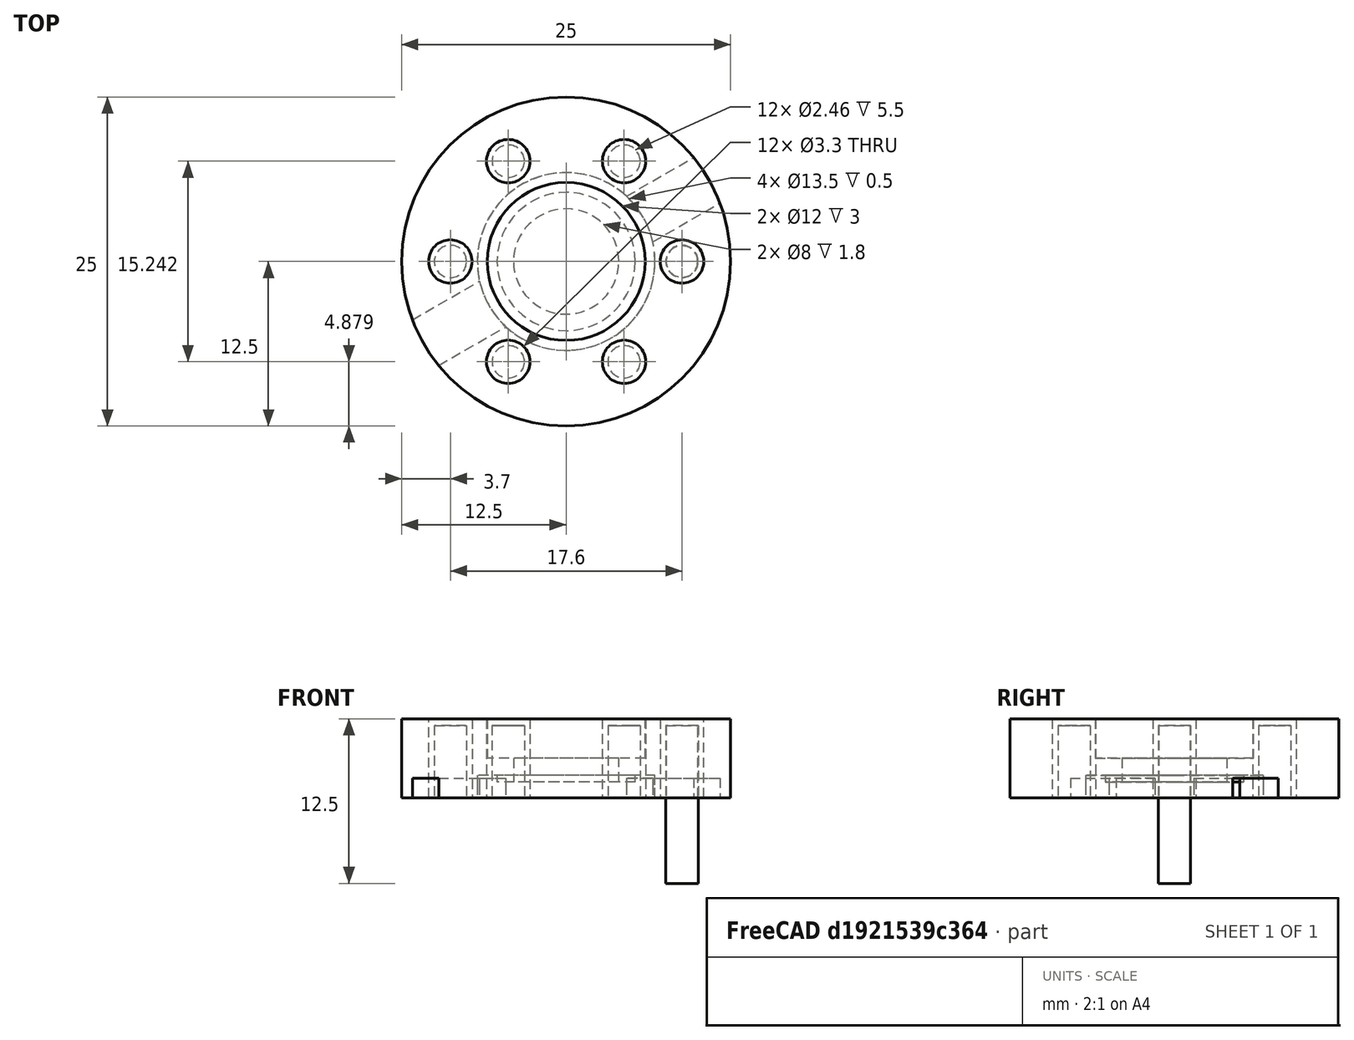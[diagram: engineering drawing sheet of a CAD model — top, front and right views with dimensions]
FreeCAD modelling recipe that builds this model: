
FCSTD DOCUMENT  (FreeCAD 1.0R1.0rc2)
Label: CFFlange_NoKnife
License: All rights reserved
LicenseURL: http://en.wikipedia.org/wiki/All_rights_reserved
objects: Part::Cylinder×32, Part::Cut×32, Part::MultiFuse×10, Part::Box×8, Part::FeaturePython×8, Part::Cone×4, Spreadsheet::Sheet×1
note: 88 computed .brp shape members not serialized (recipe doc carries the construction recipe); baked Part::Feature solids carry a one-line shape summary decoded from their .brp

FEATURE [Part::Box] Box  label="Cube"
  AttacherType = Attacher::AttachEngine3D
  Height = 1.5
  Length = 6.75
  Placement = pos=(6.25,-2,0) rot=(0,0,1;0rad)
  Width = 4
  expr: .Placement.Base.x = <<ConflatFlange001>>.cf_sealrecess / 2 - 0.5
  expr: .Placement.Base.y = -2
  expr: Length = (<<ConflatFlange001>>.cf_od - <<ConflatFlange001>>.cf_sealrecess) / 2 + 1
FEATURE [Part::Box] Box001  label="Cube001"
  AttacherType = Attacher::AttachEngine3D
  Height = 1.5
  Length = 6.75
  Placement = pos=(-13,-2,0) rot=(0,0,1;0rad)
  Width = 4
  expr: .Placement.Base.x = -<<ConflatFlange001>>.cf_sealrecess / 2 + 0.5 - ((<<ConflatFlange001>>.cf_od - <<ConflatFlange001>>.cf_sealrecess) / 2 + 1)
  expr: .Placement.Base.y = -2
  expr: Length = (<<ConflatFlange001>>.cf_od - <<ConflatFlange001>>.cf_sealrecess) / 2 + 1
FEATURE [Part::Cone] Cone
  Angle = 360
  AttacherType = Attacher::AttachEngine3D
  Height = 0.22
  Radius1 = 5.25
  Radius2 = 6.75
  expr: Height = 1.2 - 0.98
  expr: Radius1 = <<ConflatFlange001>>.cf_knife / 2
  expr: Radius2 = <<ConflatFlange001>>.cf_sealrecess / 2
FEATURE [Part::Cylinder] Cylinder  label="Blank"
  Angle = 360
  AttacherType = Attacher::AttachEngine3D
  FirstAngle = 0
  Height = 6
  Radius = 12.5
  SecondAngle = 0
  expr: Height = <<ConflatFlange001>>.cf_thickness
  expr: Radius = <<ConflatFlange001>>.cf_od / 2
FEATURE [Part::Cylinder] Cylinder001  label="SealRecess"
  Angle = 360
  AttacherType = Attacher::AttachEngine3D
  FirstAngle = 0
  Height = 1.2
  Radius = 6.75
  SecondAngle = 0
  expr: Radius = <<ConflatFlange001>>.cf_sealrecess / 2
FEATURE [Part::Cut] Cut
  Base = -> Cylinder
  Tool = -> Cylinder001
FEATURE [Part::Cylinder] Cylinder002  label="Cylinder"
  Angle = 360
  AttacherType = Attacher::AttachEngine3D
  FirstAngle = 0
  Height = 0.22
  Radius = 5.25
  SecondAngle = 0
  expr: Height = 1.2 - 0.98
  expr: Radius = <<ConflatFlange001>>.cf_knife / 2
FEATURE [Part::Cut] Cut001  label="KnifeEdge"
  Base = -> Cone
  Placement = pos=(0,0,0.98) rot=(0,0,1;0rad)
  Tool = -> Cylinder002
FEATURE [Part::Cylinder] Cylinder003
  Angle = 360
  AttacherType = Attacher::AttachEngine3D
  FirstAngle = 0
  Height = 6
  Placement = pos=(8.8,0,0) rot=(0,0,1;0rad)
  Radius = 1.65
  SecondAngle = 0
  expr: .Placement.Base.x = <<ConflatFlange001>>.cf_boltcircle / 2
  expr: Height = <<ConflatFlange001>>.cf_thickness
  expr: Radius = <<ConflatFlange001>>.cf_boltdia / 2
FEATURE [Part::FeaturePython] Array  label="BoltHoleArray"  # Draft array (typed FeaturePython)
  AlwaysSyncPlacement = false
  Angle = 360
  ArrayType = 1
  Axis = (0,0,1)
  Base = -> Cylinder003
  Center = (0,0,0)
  Count = 6
  ExpandArray = false
  Fuse = false
  IntervalAxis = (0,0,0)
  IntervalX = (50,0,0)
  IntervalY = (0,50,0)
  IntervalZ = (0,0,50)
  NumberCircles = 3
  NumberPolar = 6
  NumberX = 2
  NumberY = 2
  NumberZ = 1
  PlacementList = 6 placements: [(8.8,0,0),(4.4,7.62102,0),(-4.4,7.62102,0),(-8.8,1.07769e-15,0),(-4.4,-7.62102,0),(4.4,-7.62102,0)]
  RadialDistance = 50
  ScaleList = (6) [(1,1,1),(1,1,1),(1,1,1),(1,1,1),(1,1,1),(1,1,1)]
  Symmetry = 1
  TangentialDistance = 25
  expr: NumberPolar = <<ConflatFlange001>>.cf_nbolts
FEATURE [Part::Cylinder] Cylinder024
  Angle = 360
  AttacherType = Attacher::AttachEngine3D
  FirstAngle = 0
  Height = 1.5
  Radius = 6.75
  SecondAngle = 0
  expr: Radius = <<ConflatFlange001>>.cf_sealrecess / 2
FEATURE [Part::MultiFuse] Fusion  label="UndrilledBlank"
  Shapes = -> [Cut,Cut001]
FEATURE [Part::Cut] Cut002  label="BlankFlange_NonRotatable_NoGrooves"
  Base = -> Fusion
  Tool = -> Array
FEATURE [Part::MultiFuse] Fusion007
  Placement = pos=(0,0,0) rot=(0,0,1;0.523599rad)
  Shapes = -> [Box001,Box]
  expr: .Placement.Rotation.Angle = 360 / (<<ConflatFlange001>>.cf_nbolts * 2)
FEATURE [Part::Cut] Cut019  label="LeakTestGrooves01"
  Base = -> Fusion007
  Tool = -> Cylinder024
FEATURE [Part::Cut] Cut020  label="BlankFlange_NonRotatable"
  Base = -> Cut002
  Tool = -> Cut019
FEATURE [Spreadsheet::Sheet] Spreadsheet001  label="ConflatFlange001"
  CF = 0
  cells = A1='CF; B1='Outside Diameter; C1='Maximum tube diameter; D1='Number of bolts; E1='Bolt hole diameter; F1='Tap hole diameter; G1='Bolt Thread (metric); H1='Bot inclination; I1='Bolt Circle; J1='Bolt position tolerance; K1='Seal recess; L1='Knife edge; M1='Pipe attachment depth; N1='Setback (inner rotatable); O1='Thickness; Q1='Calculated Quantities; A2==hiddenref(.CF.String); B2(cf_od)==.B3; C2(cf_maxtubedia)==.C3; D2(cf_nbolts)==.D3; E2(cf_boltdia)==.E3; F2(cf_tapdia)==.F3; G2(cf_boltm)==.G3; H2(cf_boltinclination)==.H3; I2(cf_boltcircle)==.I3; J2(cf_bolttolerance)==.J3; K2(cf_sealrecess)==.K3; L2(cf_knife)==.L3; M2(cf_pipedepth)==.M3; N2(cf_setbackrot)==.N3; O2(cf_thickness)==.O3; Q2='Knife edge width; R2(cf__kfwidth)==(cf_sealrecess - cf_knife) / 2; A3='10; B3=25; C3=12; D3=6; E3=3.3; F3=2.39; G3=3; H3=0.5; I3=17.6; J3=0.1; K3=13.5; L3=10.5; M3=3; N3=0; O3=6; Q3='Knife height; R3(cf__kfheight)==tan(20 * 3.14 / 180) * cf__kfwidth; A4='16; B4=33.8; C4=19.4; D4=6; E4=4.4; F4=3.14; G4=4; H4=0.7; I4=27; J4=0.1; K4=21.4; L4=18.3; M4=3.3; N4=5.9; O4=7; A5='25; B5=54; C5=25.8; D5=4; E5=6.8; F5=4.77; G5=6; H5=1; I5=41.3; J5=0.2; K5=33; L5=27.7; M5=4.3; N5=6; O5=11.5; A6='40; B6=69.9; C6=44.5; D6=6; E6=6.8; F6=4.77; G6=6; H6=1; I6=58.7; J6=0.2; K6=48.3; L6=41.9; M6=4.3; N6=7.7; O6=12.5; A7='50; B7=85.7; C7=51; D7=8; E7=8.4; F7=6.47; G7=8; H7=1.25; I7=72.4; J7=0.2; K7=61.8; L7=55.9; M7=4.9; N7=9.7; O7=16; A8='63; B8=114.3; C8=70; D8=8; E8=8.4; F8=6.47; G8=8; H8=1.25; I8=92.2; J8=0.2; K8=82.5; L8=77.2; M8=6.4; N8=12.7; O8=17; A9='75; B9=117.4; C9=76.2; D9=10; E9=8.4; F9=6.47; G9=8; H9=1.25; I9=102.3; J9=0.2; K9=91.6; L9=85.2; M9=6.5; N9=13; O9=17.5; A10='100; B10=152.4; C10=108; D10=16; E10=8.4; F10=6.47; G10=8; H10=1.25; I10=130.3; J10=0.2; K10=120.6; L10=115.3; M10=7.2; N10=14.3; O10=19.5; A11='125; B11=171.5; C11=127; D11=18; E11=8.4; F11=6.47; G11=8; H11=1.25; I11=151.6; J11=0.2; K11=141.8; L11=136.3; M11=7.2; N11=14.3; O11=21; A12='160; B12=203.2; C12=159; D12=20; E12=8.4; F12=6.47; G12=8; H12=1.25; I12=181; J12=0.2; K12=171.4; L12=166.1; M12=8; N12=15.9; O12=21; A13='200; B13=254; C13=206; D13=24; E13=8.4; F13=6.47; G13=8; H13=1.25; I13=231.8; J13=0.2; K13=222.2; L13=216.9; M13=8.6; N13=17.2; O13=24; +99 more cells
  expr: .CF.Enum = cells[<<A3:|>>]
  expr: .cells.Bind.B2.O2 = tuple(.cells; <<B>> + str(hiddenref(CF) + 3); <<O>> + str(hiddenref(CF) + 3))
FEATURE [Part::Cylinder] Cylinder025
  Angle = 360
  AttacherType = Attacher::AttachEngine3D
  FirstAngle = 0
  Height = 0.72
  Radius = 6.75
  SecondAngle = 0
  expr: Height = 0.22 + <<ConflatFlange001>>.oring_depth
  expr: Radius = <<ConflatFlange001>>.cf_sealrecess / 2
FEATURE [Part::Cylinder] Cylinder026
  Angle = 360
  AttacherType = Attacher::AttachEngine3D
  FirstAngle = 0
  Height = 0.72
  Radius = 5.25
  SecondAngle = 0
  expr: Height = 0.22 + <<ConflatFlange001>>.oring_depth
  expr: Radius = <<ConflatFlange001>>.cf_knife / 2
FEATURE [Part::Cut] Cut021
  Base = -> Cylinder025
  Placement = pos=(0,0,0.98) rot=(0,0,1;0rad)
  Tool = -> Cylinder026
FEATURE [Part::Cut] Cut022  label="Blank_NonRotateable_ORing"
  Base = -> Cut020
  Tool = -> Cut021
FEATURE [Part::Cylinder] Cylinder018
  Angle = 360
  AttacherType = Attacher::AttachEngine3D
  FirstAngle = 0
  Height = 3
  Placement = pos=(0,0,3) rot=(0,0,1;0rad)
  Radius = 6
  SecondAngle = 0
  expr: .Placement.Base.z = <<ConflatFlange001>>.cf_pipedepth
  expr: Height = <<ConflatFlange001>>.cf_thickness - <<ConflatFlange001>>.cf_pipedepth
  expr: Radius = <<ConflatFlange001>>.cf_maxtubedia / 2
FEATURE [Part::Cylinder] Cylinder019
  Angle = 360
  AttacherType = Attacher::AttachEngine3D
  FirstAngle = 0
  Height = 6
  Radius = 4
  SecondAngle = 0
  expr: Height = <<ConflatFlange001>>.cf_thickness
  expr: Radius = <<ConflatFlange001>>.cf_maxtubedia / 2 - <<ConflatFlange001>>.cf_pipe_wallwidth
FEATURE [Part::MultiFuse] Fusion006
  Shapes = -> [Cylinder019,Cylinder018]
FEATURE [Part::Box] Box002  label="Cube002"
  AttacherType = Attacher::AttachEngine3D
  Height = 1.5
  Length = 6.75
  Placement = pos=(6.25,-2,0) rot=(0,0,1;0rad)
  Width = 4
  expr: .Placement.Base.x = <<ConflatFlange001>>.cf_sealrecess / 2 - 0.5
  expr: .Placement.Base.y = -2
  expr: Length = (<<ConflatFlange001>>.cf_od - <<ConflatFlange001>>.cf_sealrecess) / 2 + 1
FEATURE [Part::Box] Box003  label="Cube003"
  AttacherType = Attacher::AttachEngine3D
  Height = 1.5
  Length = 6.75
  Placement = pos=(-13,-2,0) rot=(0,0,1;0rad)
  Width = 4
  expr: .Placement.Base.x = -<<ConflatFlange001>>.cf_sealrecess / 2 + 0.5 - ((<<ConflatFlange001>>.cf_od - <<ConflatFlange001>>.cf_sealrecess) / 2 + 1)
  expr: .Placement.Base.y = -2
  expr: Length = (<<ConflatFlange001>>.cf_od - <<ConflatFlange001>>.cf_sealrecess) / 2 + 1
FEATURE [Part::Cone] Cone001
  Angle = 360
  AttacherType = Attacher::AttachEngine3D
  Height = 0.22
  Radius1 = 5.25
  Radius2 = 6.75
  expr: Height = 1.2 - 0.98
  expr: Radius1 = <<ConflatFlange001>>.cf_knife / 2
  expr: Radius2 = <<ConflatFlange001>>.cf_sealrecess / 2
FEATURE [Part::Cylinder] Cylinder027  label="Blank001"
  Angle = 360
  AttacherType = Attacher::AttachEngine3D
  FirstAngle = 0
  Height = 6
  Radius = 12.5
  SecondAngle = 0
  expr: Height = <<ConflatFlange001>>.cf_thickness
  expr: Radius = <<ConflatFlange001>>.cf_od / 2
FEATURE [Part::Cylinder] Cylinder028  label="SealRecess001"
  Angle = 360
  AttacherType = Attacher::AttachEngine3D
  FirstAngle = 0
  Height = 1.2
  Radius = 6.75
  SecondAngle = 0
  expr: Radius = <<ConflatFlange001>>.cf_sealrecess / 2
FEATURE [Part::Cut] Cut023
  Base = -> Cylinder027
  Tool = -> Cylinder028
FEATURE [Part::Cylinder] Cylinder029
  Angle = 360
  AttacherType = Attacher::AttachEngine3D
  FirstAngle = 0
  Height = 0.22
  Radius = 5.25
  SecondAngle = 0
  expr: Height = 1.2 - 0.98
  expr: Radius = <<ConflatFlange001>>.cf_knife / 2
FEATURE [Part::Cut] Cut024  label="KnifeEdge001"
  Base = -> Cone001
  Placement = pos=(0,0,0.98) rot=(0,0,1;0rad)
  Tool = -> Cylinder029
FEATURE [Part::Cylinder] Cylinder030
  Angle = 360
  AttacherType = Attacher::AttachEngine3D
  FirstAngle = 0
  Height = 6
  Placement = pos=(8.8,0,0) rot=(0,0,1;0rad)
  Radius = 1.65
  SecondAngle = 0
  expr: .Placement.Base.x = <<ConflatFlange001>>.cf_boltcircle / 2
  expr: Height = <<ConflatFlange001>>.cf_thickness
  expr: Radius = <<ConflatFlange001>>.cf_boltdia / 2
FEATURE [Part::FeaturePython] Array001  label="BoltHoleArray001"  # Draft array (typed FeaturePython)
  AlwaysSyncPlacement = false
  Angle = 360
  ArrayType = 1
  Axis = (0,0,1)
  Base = -> Cylinder030
  Center = (0,0,0)
  Count = 6
  ExpandArray = false
  Fuse = false
  IntervalAxis = (0,0,0)
  IntervalX = (50,0,0)
  IntervalY = (0,50,0)
  IntervalZ = (0,0,50)
  NumberCircles = 3
  NumberPolar = 6
  NumberX = 2
  NumberY = 2
  NumberZ = 1
  PlacementList = 6 placements: [(8.8,0,0),(4.4,7.62102,0),(-4.4,7.62102,0),(-8.8,1.07769e-15,0),(-4.4,-7.62102,0),(4.4,-7.62102,0)]
  RadialDistance = 50
  ScaleList = (6) [(1,1,1),(1,1,1),(1,1,1),(1,1,1),(1,1,1),(1,1,1)]
  Symmetry = 1
  TangentialDistance = 25
  expr: NumberPolar = <<ConflatFlange001>>.cf_nbolts
FEATURE [Part::Cylinder] Cylinder031
  Angle = 360
  AttacherType = Attacher::AttachEngine3D
  FirstAngle = 0
  Height = 1.5
  Radius = 6.75
  SecondAngle = 0
  expr: Radius = <<ConflatFlange001>>.cf_sealrecess / 2
FEATURE [Part::Cylinder] Cylinder032
  Angle = 360
  AttacherType = Attacher::AttachEngine3D
  FirstAngle = 0
  Height = 0.72
  Radius = 6.75
  SecondAngle = 0
  expr: Height = 0.22 + <<ConflatFlange001>>.oring_depth
  expr: Radius = <<ConflatFlange001>>.cf_sealrecess / 2
FEATURE [Part::Cylinder] Cylinder033
  Angle = 360
  AttacherType = Attacher::AttachEngine3D
  FirstAngle = 0
  Height = 0.72
  Radius = 5.25
  SecondAngle = 0
  expr: Height = 0.22 + <<ConflatFlange001>>.oring_depth
  expr: Radius = <<ConflatFlange001>>.cf_knife / 2
FEATURE [Part::Cut] Cut028
  Base = -> Cylinder032
  Placement = pos=(0,0,0.98) rot=(0,0,1;0rad)
  Tool = -> Cylinder033
FEATURE [Part::MultiFuse] Fusion008  label="UndrilledBlank001"
  Shapes = -> [Cut023,Cut024]
FEATURE [Part::Cut] Cut025  label="BlankFlange_NonRotatable_NoGrooves001"
  Base = -> Fusion008
  Tool = -> Array001
FEATURE [Part::MultiFuse] Fusion009
  Placement = pos=(0,0,0) rot=(0,0,1;0.523599rad)
  Shapes = -> [Box003,Box002]
  expr: .Placement.Rotation.Angle = 360 / (<<ConflatFlange001>>.cf_nbolts * 2)
FEATURE [Part::Cut] Cut026  label="LeakTestGrooves002"
  Base = -> Fusion009
  Tool = -> Cylinder031
FEATURE [Part::Cut] Cut027  label="BlankFlange_NonRotatable001"
  Base = -> Cut025
  Tool = -> Cut026
FEATURE [Part::Cut] Cut029  label="Blank_NonRotateable_ORing001"
  Base = -> Cut027
  Tool = -> Cut028
FEATURE [Part::Cut] Cut030  label="Blank_NonRotateable_Weld_ORing"
  Base = -> Cut029
  Tool = -> Fusion006
FEATURE [Part::Box] Box004  label="Cube004"
  AttacherType = Attacher::AttachEngine3D
  Height = 1.5
  Length = 6.75
  Placement = pos=(6.25,-2,0) rot=(0,0,1;0rad)
  Width = 4
  expr: .Placement.Base.x = <<ConflatFlange001>>.cf_sealrecess / 2 - 0.5
  expr: .Placement.Base.y = -2
  expr: Length = (<<ConflatFlange001>>.cf_od - <<ConflatFlange001>>.cf_sealrecess) / 2 + 1
FEATURE [Part::Box] Box005  label="Cube005"
  AttacherType = Attacher::AttachEngine3D
  Height = 1.5
  Length = 6.75
  Placement = pos=(-13,-2,0) rot=(0,0,1;0rad)
  Width = 4
  expr: .Placement.Base.x = -<<ConflatFlange001>>.cf_sealrecess / 2 + 0.5 - ((<<ConflatFlange001>>.cf_od - <<ConflatFlange001>>.cf_sealrecess) / 2 + 1)
  expr: .Placement.Base.y = -2
  expr: Length = (<<ConflatFlange001>>.cf_od - <<ConflatFlange001>>.cf_sealrecess) / 2 + 1
FEATURE [Part::Cone] Cone002
  Angle = 360
  AttacherType = Attacher::AttachEngine3D
  Height = 0.22
  Radius1 = 5.25
  Radius2 = 6.75
  expr: Height = 1.2 - 0.98
  expr: Radius1 = <<ConflatFlange001>>.cf_knife / 2
  expr: Radius2 = <<ConflatFlange001>>.cf_sealrecess / 2
FEATURE [Part::Cylinder] Cylinder034  label="Blank002"
  Angle = 360
  AttacherType = Attacher::AttachEngine3D
  FirstAngle = 0
  Height = 6
  Radius = 12.5
  SecondAngle = 0
  expr: Height = <<ConflatFlange001>>.cf_thickness
  expr: Radius = <<ConflatFlange001>>.cf_od / 2
FEATURE [Part::Cylinder] Cylinder035  label="SealRecess002"
  Angle = 360
  AttacherType = Attacher::AttachEngine3D
  FirstAngle = 0
  Height = 1.2
  Radius = 6.75
  SecondAngle = 0
  expr: Radius = <<ConflatFlange001>>.cf_sealrecess / 2
FEATURE [Part::Cut] Cut031
  Base = -> Cylinder034
  Tool = -> Cylinder035
FEATURE [Part::Cylinder] Cylinder036
  Angle = 360
  AttacherType = Attacher::AttachEngine3D
  FirstAngle = 0
  Height = 0.22
  Radius = 5.25
  SecondAngle = 0
  expr: Height = 1.2 - 0.98
  expr: Radius = <<ConflatFlange001>>.cf_knife / 2
FEATURE [Part::Cut] Cut032  label="KnifeEdge002"
  Base = -> Cone002
  Placement = pos=(0,0,0.98) rot=(0,0,1;0rad)
  Tool = -> Cylinder036
FEATURE [Part::Cylinder] Cylinder037
  Angle = 360
  AttacherType = Attacher::AttachEngine3D
  FirstAngle = 0
  Height = 5.5
  Placement = pos=(8.8,0,0) rot=(0,0,1;0rad)
  Radius = 1.195
  SecondAngle = 0
  expr: .Placement.Base.x = <<ConflatFlange001>>.cf_boltcircle / 2
  expr: Height = <<ConflatFlange001>>.cf_thickness - 0.5
  expr: Radius = <<ConflatFlange001>>.cf_tapdia / 2
FEATURE [Part::FeaturePython] Array002  label="BoltHoleArray002"  # Draft array (typed FeaturePython)
  AlwaysSyncPlacement = false
  Angle = 360
  ArrayType = 1
  Axis = (0,0,1)
  Base = -> Cylinder037
  Center = (0,0,0)
  Count = 6
  ExpandArray = false
  Fuse = false
  IntervalAxis = (0,0,0)
  IntervalX = (50,0,0)
  IntervalY = (0,50,0)
  IntervalZ = (0,0,50)
  NumberCircles = 3
  NumberPolar = 6
  NumberX = 2
  NumberY = 2
  NumberZ = 1
  PlacementList = 6 placements: [(8.8,0,0),(4.4,7.62102,0),(-4.4,7.62102,0),(-8.8,1.07769e-15,0),(-4.4,-7.62102,0),(4.4,-7.62102,0)]
  RadialDistance = 50
  ScaleList = (6) [(1,1,1),(1,1,1),(1,1,1),(1,1,1),(1,1,1),(1,1,1)]
  Symmetry = 1
  TangentialDistance = 25
  expr: NumberPolar = <<ConflatFlange001>>.cf_nbolts
FEATURE [Part::Cylinder] Cylinder038
  Angle = 360
  AttacherType = Attacher::AttachEngine3D
  FirstAngle = 0
  Height = 1.5
  Radius = 6.75
  SecondAngle = 0
  expr: Radius = <<ConflatFlange001>>.cf_sealrecess / 2
FEATURE [Part::Cylinder] Cylinder039
  Angle = 360
  AttacherType = Attacher::AttachEngine3D
  FirstAngle = 0
  Height = 0.72
  Radius = 6.75
  SecondAngle = 0
  expr: Height = 0.22 + <<ConflatFlange001>>.oring_depth
  expr: Radius = <<ConflatFlange001>>.cf_sealrecess / 2
FEATURE [Part::Cylinder] Cylinder040
  Angle = 360
  AttacherType = Attacher::AttachEngine3D
  FirstAngle = 0
  Height = 0.72
  Radius = 5.25
  SecondAngle = 0
  expr: Height = 0.22 + <<ConflatFlange001>>.oring_depth
  expr: Radius = <<ConflatFlange001>>.cf_knife / 2
FEATURE [Part::Cut] Cut036
  Base = -> Cylinder039
  Placement = pos=(0,0,0.98) rot=(0,0,1;0rad)
  Tool = -> Cylinder040
FEATURE [Part::MultiFuse] Fusion010  label="UndrilledBlank002"
  Shapes = -> [Cut031,Cut032]
FEATURE [Part::Cut] Cut033  label="BlankFlange_NonRotatable_NoGrooves002"
  Base = -> Fusion010
  Tool = -> Array002
FEATURE [Part::MultiFuse] Fusion011
  Placement = pos=(0,0,0) rot=(0,0,1;0.523599rad)
  Shapes = -> [Box005,Box004]
  expr: .Placement.Rotation.Angle = 360 / (<<ConflatFlange001>>.cf_nbolts * 2)
FEATURE [Part::Cut] Cut034  label="LeakTestGrooves003"
  Base = -> Fusion011
  Tool = -> Cylinder038
FEATURE [Part::Cut] Cut035  label="BlankFlange_NonRotatable002"
  Base = -> Cut033
  Tool = -> Cut034
FEATURE [Part::Cut] Cut037  label="Blank_NonRotateable_ORing_Tapped_Model"
  Base = -> Cut035
  Tool = -> Cut036
FEATURE [Part::FeaturePython] ScrewTap  label="3x12-ScrewTap"  # WARN: FeaturePython — macro-defined, semantics opaque (R4)
  Diameter = 29
  DiameterCustom = 3
  Invert = false
  LeftHanded = false
  Length = 12
  MatchOuter = false
  PitchCustom = 0.5
  Placement = pos=(8.8,0,5.5) rot=(0,0,1;0rad)
  Thread = false
  Type = 2
  expr: .Placement.Base.x = <<ConflatFlange001>>.cf_boltcircle / 2
  expr: .Placement.Base.z = <<ConflatFlange001>>.cf_thickness - 0.5
  expr: DiameterCustom = <<ConflatFlange001>>.cf_boltm
  expr: Length = <<ConflatFlange001>>.cf_thickness * 2
  expr: PitchCustom = <<ConflatFlange001>>.cf_boltinclination
FEATURE [Part::FeaturePython] Array003  label="ThreadCut"  # Draft array (typed FeaturePython)
  AlwaysSyncPlacement = false
  Angle = 360
  ArrayType = 1
  Axis = (0,0,1)
  Base = -> ScrewTap
  Center = (0,0,0)
  Count = 6
  ExpandArray = false
  Fuse = false
  IntervalAxis = (0,0,0)
  IntervalX = (50,0,0)
  IntervalY = (0,50,0)
  IntervalZ = (0,0,50)
  NumberCircles = 3
  NumberPolar = 6
  NumberX = 2
  NumberY = 2
  NumberZ = 1
  PlacementList = 6 placements: [(8.8,0,5.5),(4.4,7.62102,5.5),(-4.4,7.62102,5.5),(-8.8,1.07769e-15,5.5),(-4.4,-7.62102,5.5),(4.4,-7.62102,5.5)]
  RadialDistance = 50
  ScaleList = (6) [(1,1,1),(1,1,1),(1,1,1),(1,1,1),(1,1,1),(1,1,1)]
  Symmetry = 1
  TangentialDistance = 25
  expr: NumberPolar = <<ConflatFlange001>>.cf_nbolts
FEATURE [Part::Cut] Cut038  label="Blank_NonRotateable_ORing_Tapped_Rendering"
  Base = -> Cut037
  Tool = -> Array003
FEATURE [Part::Box] Box006  label="Cube006"
  AttacherType = Attacher::AttachEngine3D
  Height = 1.5
  Length = 6.75
  Placement = pos=(6.25,-2,0) rot=(0,0,1;0rad)
  Width = 4
  expr: .Placement.Base.x = <<ConflatFlange001>>.cf_sealrecess / 2 - 0.5
  expr: .Placement.Base.y = -2
  expr: Length = (<<ConflatFlange001>>.cf_od - <<ConflatFlange001>>.cf_sealrecess) / 2 + 1
FEATURE [Part::Box] Box007  label="Cube007"
  AttacherType = Attacher::AttachEngine3D
  Height = 1.5
  Length = 6.75
  Placement = pos=(-13,-2,0) rot=(0,0,1;0rad)
  Width = 4
  expr: .Placement.Base.x = -<<ConflatFlange001>>.cf_sealrecess / 2 + 0.5 - ((<<ConflatFlange001>>.cf_od - <<ConflatFlange001>>.cf_sealrecess) / 2 + 1)
  expr: .Placement.Base.y = -2
  expr: Length = (<<ConflatFlange001>>.cf_od - <<ConflatFlange001>>.cf_sealrecess) / 2 + 1
FEATURE [Part::Cone] Cone003
  Angle = 360
  AttacherType = Attacher::AttachEngine3D
  Height = 0.22
  Radius1 = 5.25
  Radius2 = 6.75
  expr: Height = 1.2 - 0.98
  expr: Radius1 = <<ConflatFlange001>>.cf_knife / 2
  expr: Radius2 = <<ConflatFlange001>>.cf_sealrecess / 2
FEATURE [Part::Cylinder] Cylinder041
  Angle = 360
  AttacherType = Attacher::AttachEngine3D
  FirstAngle = 0
  Height = 3
  Placement = pos=(0,0,3) rot=(0,0,1;0rad)
  Radius = 6
  SecondAngle = 0
  expr: .Placement.Base.z = <<ConflatFlange001>>.cf_pipedepth
  expr: Height = <<ConflatFlange001>>.cf_thickness - <<ConflatFlange001>>.cf_pipedepth
  expr: Radius = <<ConflatFlange001>>.cf_maxtubedia / 2
FEATURE [Part::Cylinder] Cylinder042
  Angle = 360
  AttacherType = Attacher::AttachEngine3D
  FirstAngle = 0
  Height = 6
  Radius = 4
  SecondAngle = 0
  expr: Height = <<ConflatFlange001>>.cf_thickness
  expr: Radius = <<ConflatFlange001>>.cf_maxtubedia / 2 - <<ConflatFlange001>>.cf_pipe_wallwidth
FEATURE [Part::Cylinder] Cylinder043  label="Blank003"
  Angle = 360
  AttacherType = Attacher::AttachEngine3D
  FirstAngle = 0
  Height = 6
  Radius = 12.5
  SecondAngle = 0
  expr: Height = <<ConflatFlange001>>.cf_thickness
  expr: Radius = <<ConflatFlange001>>.cf_od / 2
FEATURE [Part::Cylinder] Cylinder044  label="SealRecess003"
  Angle = 360
  AttacherType = Attacher::AttachEngine3D
  FirstAngle = 0
  Height = 1.2
  Radius = 6.75
  SecondAngle = 0
  expr: Radius = <<ConflatFlange001>>.cf_sealrecess / 2
FEATURE [Part::Cut] Cut039
  Base = -> Cylinder043
  Tool = -> Cylinder044
FEATURE [Part::Cylinder] Cylinder045
  Angle = 360
  AttacherType = Attacher::AttachEngine3D
  FirstAngle = 0
  Height = 0.22
  Radius = 5.25
  SecondAngle = 0
  expr: Height = 1.2 - 0.98
  expr: Radius = <<ConflatFlange001>>.cf_knife / 2
FEATURE [Part::Cut] Cut040  label="KnifeEdge003"
  Base = -> Cone003
  Placement = pos=(0,0,0.98) rot=(0,0,1;0rad)
  Tool = -> Cylinder045
FEATURE [Part::Cylinder] Cylinder046
  Angle = 360
  AttacherType = Attacher::AttachEngine3D
  FirstAngle = 0
  Height = 5.5
  Placement = pos=(8.8,0,0) rot=(0,0,1;0rad)
  Radius = 1.195
  SecondAngle = 0
  expr: .Placement.Base.x = <<ConflatFlange001>>.cf_boltcircle / 2
  expr: Height = <<ConflatFlange001>>.cf_thickness - 0.5
  expr: Radius = <<ConflatFlange001>>.cf_tapdia / 2
FEATURE [Part::FeaturePython] Array004  label="BoltHoleArray003"  # Draft array (typed FeaturePython)
  AlwaysSyncPlacement = false
  Angle = 360
  ArrayType = 1
  Axis = (0,0,1)
  Base = -> Cylinder046
  Center = (0,0,0)
  Count = 6
  ExpandArray = false
  Fuse = false
  IntervalAxis = (0,0,0)
  IntervalX = (50,0,0)
  IntervalY = (0,50,0)
  IntervalZ = (0,0,50)
  NumberCircles = 3
  NumberPolar = 6
  NumberX = 2
  NumberY = 2
  NumberZ = 1
  PlacementList = 6 placements: [(8.8,0,0),(4.4,7.62102,0),(-4.4,7.62102,0),(-8.8,1.07769e-15,0),(-4.4,-7.62102,0),(4.4,-7.62102,0)]
  RadialDistance = 50
  ScaleList = (6) [(1,1,1),(1,1,1),(1,1,1),(1,1,1),(1,1,1),(1,1,1)]
  Symmetry = 1
  TangentialDistance = 25
  expr: NumberPolar = <<ConflatFlange001>>.cf_nbolts
FEATURE [Part::Cylinder] Cylinder047
  Angle = 360
  AttacherType = Attacher::AttachEngine3D
  FirstAngle = 0
  Height = 1.5
  Radius = 6.75
  SecondAngle = 0
  expr: Radius = <<ConflatFlange001>>.cf_sealrecess / 2
FEATURE [Part::Cylinder] Cylinder048
  Angle = 360
  AttacherType = Attacher::AttachEngine3D
  FirstAngle = 0
  Height = 0.72
  Radius = 6.75
  SecondAngle = 0
  expr: Height = 0.22 + <<ConflatFlange001>>.oring_depth
  expr: Radius = <<ConflatFlange001>>.cf_sealrecess / 2
FEATURE [Part::Cylinder] Cylinder049
  Angle = 360
  AttacherType = Attacher::AttachEngine3D
  FirstAngle = 0
  Height = 0.72
  Radius = 5.25
  SecondAngle = 0
  expr: Height = 0.22 + <<ConflatFlange001>>.oring_depth
  expr: Radius = <<ConflatFlange001>>.cf_knife / 2
FEATURE [Part::Cut] Cut044
  Base = -> Cylinder048
  Placement = pos=(0,0,0.98) rot=(0,0,1;0rad)
  Tool = -> Cylinder049
FEATURE [Part::MultiFuse] Fusion012
  Shapes = -> [Cylinder042,Cylinder041]
FEATURE [Part::MultiFuse] Fusion013  label="UndrilledBlank003"
  Shapes = -> [Cut039,Cut040]
FEATURE [Part::Cut] Cut041  label="BlankFlange_NonRotatable_NoGrooves003"
  Base = -> Fusion013
  Tool = -> Array004
FEATURE [Part::MultiFuse] Fusion014
  Placement = pos=(0,0,0) rot=(0,0,1;0.523599rad)
  Shapes = -> [Box007,Box006]
  expr: .Placement.Rotation.Angle = 360 / (<<ConflatFlange001>>.cf_nbolts * 2)
FEATURE [Part::Cut] Cut042  label="LeakTestGrooves004"
  Base = -> Fusion014
  Tool = -> Cylinder047
FEATURE [Part::Cut] Cut043  label="BlankFlange_NonRotatable003"
  Base = -> Cut041
  Tool = -> Cut042
FEATURE [Part::Cut] Cut045  label="Blank_NonRotateable_ORing002"
  Base = -> Cut043
  Tool = -> Cut044
FEATURE [Part::Cut] Cut046  label="Blank_NonRotateable_Weld_ORing_Tapped_Model"
  Base = -> Cut045
  Tool = -> Fusion012
FEATURE [Part::FeaturePython] ScrewTap001  label="3x12-ScrewTap001"  # WARN: FeaturePython — macro-defined, semantics opaque (R4)
  Diameter = 29
  DiameterCustom = 3
  Invert = false
  LeftHanded = false
  Length = 12
  MatchOuter = false
  PitchCustom = 0.5
  Placement = pos=(8.8,0,5.5) rot=(0,0,1;0rad)
  Thread = false
  Type = 2
  expr: .Placement.Base.x = <<ConflatFlange001>>.cf_boltcircle / 2
  expr: .Placement.Base.z = <<ConflatFlange001>>.cf_thickness - 0.5
  expr: DiameterCustom = <<ConflatFlange001>>.cf_boltm
  expr: Length = <<ConflatFlange001>>.cf_thickness * 2
  expr: PitchCustom = <<ConflatFlange001>>.cf_boltinclination
FEATURE [Part::FeaturePython] Array005  label="ThreadCut001"  # Draft array (typed FeaturePython)
  AlwaysSyncPlacement = false
  Angle = 360
  ArrayType = 1
  Axis = (0,0,1)
  Base = -> ScrewTap001
  Center = (0,0,0)
  Count = 6
  ExpandArray = false
  Fuse = false
  IntervalAxis = (0,0,0)
  IntervalX = (50,0,0)
  IntervalY = (0,50,0)
  IntervalZ = (0,0,50)
  NumberCircles = 3
  NumberPolar = 6
  NumberX = 2
  NumberY = 2
  NumberZ = 1
  PlacementList = 6 placements: [(8.8,0,5.5),(4.4,7.62102,5.5),(-4.4,7.62102,5.5),(-8.8,1.07769e-15,5.5),(-4.4,-7.62102,5.5),(4.4,-7.62102,5.5)]
  RadialDistance = 50
  ScaleList = (6) [(1,1,1),(1,1,1),(1,1,1),(1,1,1),(1,1,1),(1,1,1)]
  Symmetry = 1
  TangentialDistance = 25
  expr: NumberPolar = <<ConflatFlange001>>.cf_nbolts
FEATURE [Part::Cut] Cut047  label="Blank_NonRotateable_Weld_ORing_Tapped_Rendering"
  Base = -> Cut046
  Tool = -> Array005
